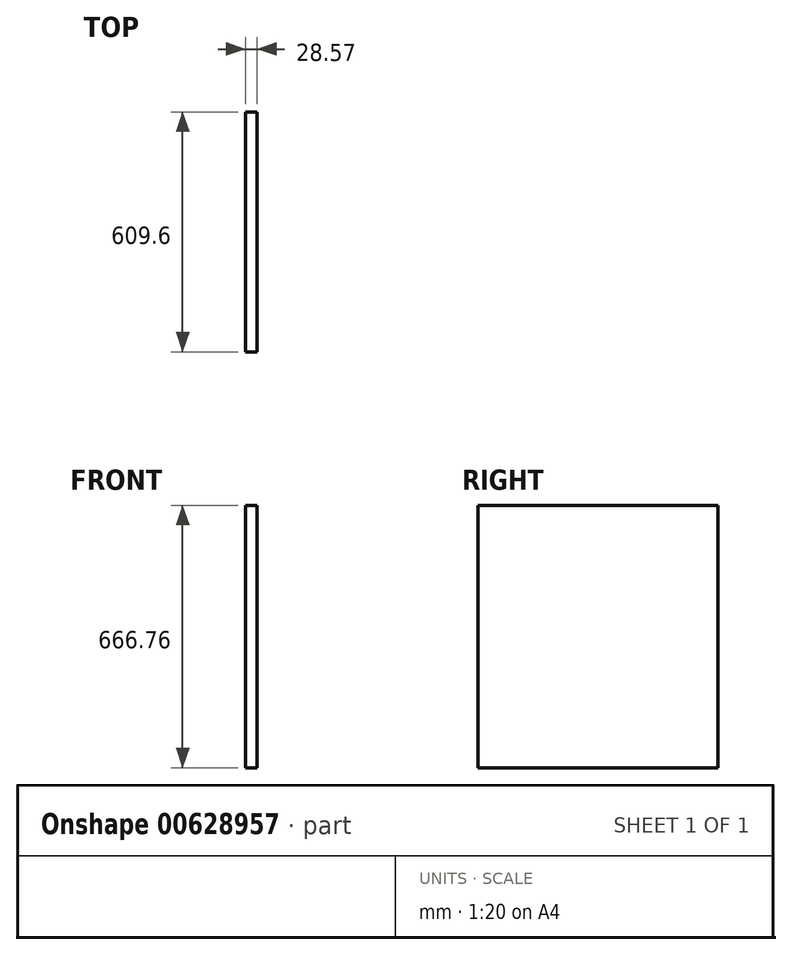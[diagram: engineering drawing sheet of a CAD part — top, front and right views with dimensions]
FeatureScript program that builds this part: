
annotation { "Feature Type Name" : "Feature", "Feature Type Description" : "" }
export const myFeature = defineFeature(function(context is Context, id is Id, definition is map)
    precondition{}
    {
        {
            var Q0;
            Q0=qCreatedBy(makeId("Right.planeOp"),FACE);
            var sketch = newSketch(context, id + "F0", { "sketchPlane" : qUnion([Q0])});
            skLineSegment(sketch, "E0.bottom", {"start": v(304.8, 333.38) * mm, "end": v(-304.8, 333.38) * mm});
            skLineSegment(sketch, "E0.top", {"start": v(304.8, -333.38) * mm, "end": v(-304.8, -333.38) * mm});
            skLineSegment(sketch, "E0.left", {"start": v(304.8, 333.38) * mm, "end": v(304.8, -333.38) * mm});
            skLineSegment(sketch, "E0.right", {"start": v(-304.8, 333.38) * mm, "end": v(-304.8, -333.38) * mm});
            skPoint(sketch, "E0.middle", {"position": v(0, 0) * mm});
            skSolve(sketch);
        }
        {
            var Q0;
            Q0=makeQuery(id+"F0.imprint","IMPRINT",FACE,{"disambiguationData":[TD([[makeQuery(id+"F0.imprint","IMPRINT",EDGE,{"derivedFrom":sQuery(id+"F0.wireOp",EDGE,"E0.bottom")}),1.0]])]});
            extrude(context, id + "F1", {"entities" : qUnion([Q0]), "depth" : 28.57 * mm, "offsetDistance" : 25.4 * mm});
        }
    });
